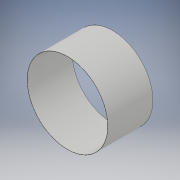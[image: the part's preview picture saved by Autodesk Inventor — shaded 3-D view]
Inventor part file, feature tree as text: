
AUTODESK INVENTOR PART (.ipt)
format: ipt  version: 2019 (Build 230136000, 136)  size: 103,936 bytes
history: native  units: mm
features: extrude x2, sketch x2
ambient origin geometry x8: Origin, YZ Plane, XZ Plane, XY Plane, X Axis, Y Axis, Z Axis, Center Point
bodies: Solid1 (feature_tree)
feature tree (4):
  extrude  "Extrusion1"  Depth=11.35mm TaperAngle=0.0deg
  extrude  "Extrusion2"  Depth=11.35mm TaperAngle=0.0deg
  sketch  "Sketch1"  dims[d0=20.37mm d1=11.35mm d2=0.0mm]
  sketch  "Sketch2"  dims[d3=20.27mm d4=11.35mm d5=0.0mm]
